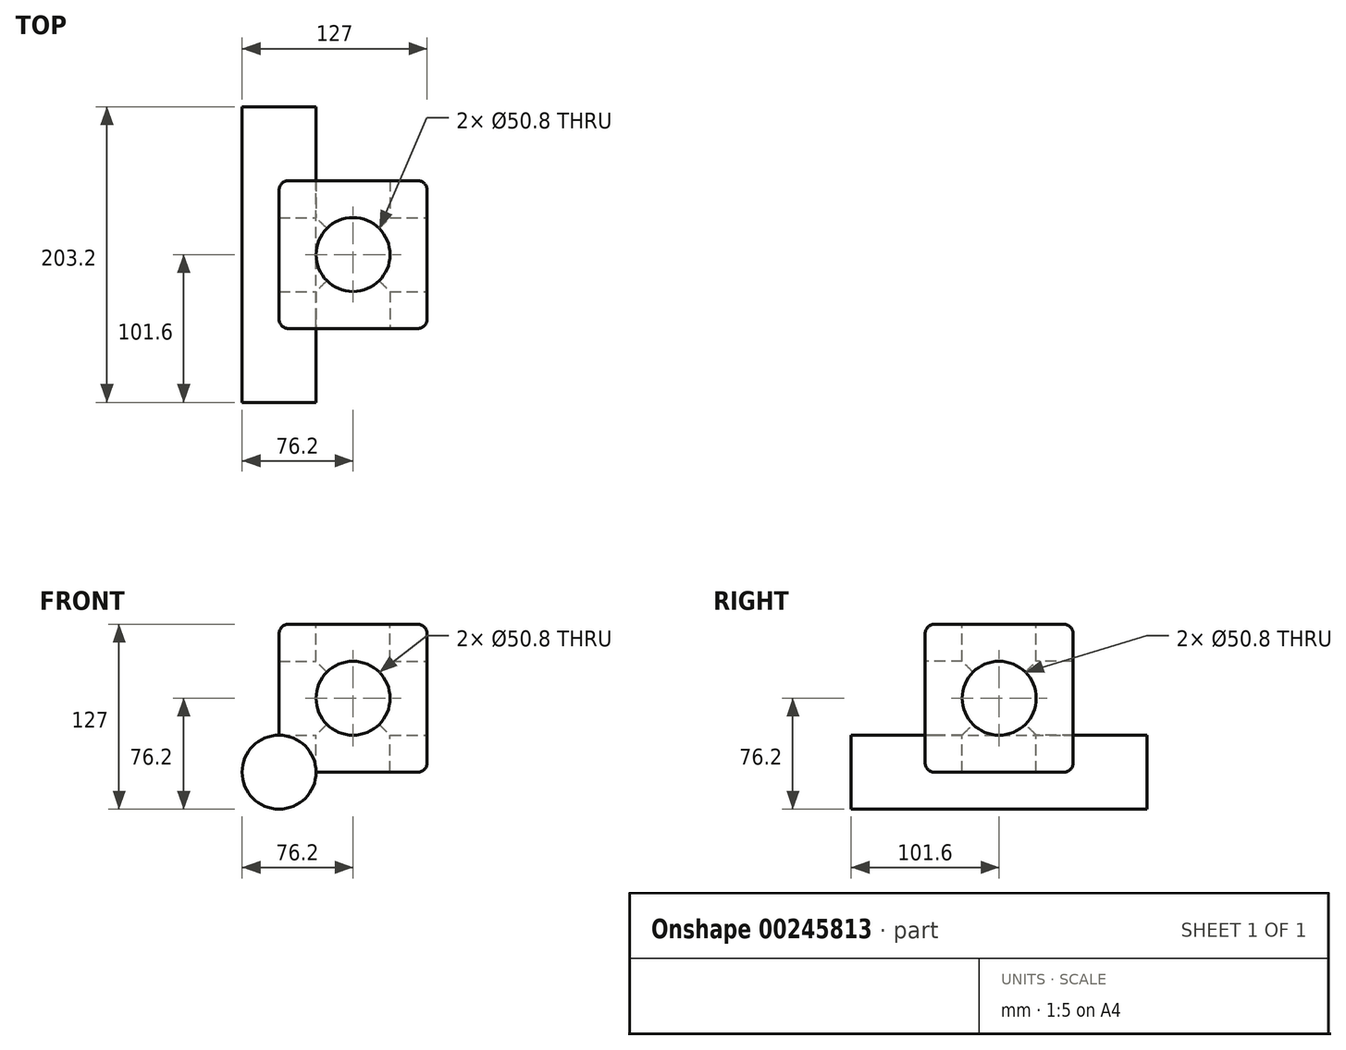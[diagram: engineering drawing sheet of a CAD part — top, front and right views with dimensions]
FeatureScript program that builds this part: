
annotation { "Feature Type Name" : "Feature", "Feature Type Description" : "" }
export const myFeature = defineFeature(function(context is Context, id is Id, definition is map)
    precondition{}
    {
        {
            var Q0;
            Q0=qCreatedBy(makeId("Front.planeOp"),FACE);
            var sketch = newSketch(context, id + "F0", { "sketchPlane" : qUnion([Q0])});
            skLineSegment(sketch, "E0", {"start": v(0, 0) * mm, "end": v(101.6, 0) * mm});
            skLineSegment(sketch, "E1", {"start": v(101.6, 0) * mm, "end": v(101.6, 101.6) * mm});
            skLineSegment(sketch, "E2", {"start": v(101.6, 101.6) * mm, "end": v(0, 101.6) * mm});
            skLineSegment(sketch, "E3", {"start": v(0, 101.6) * mm, "end": v(0, 0) * mm});
            skSolve(sketch);
        }
        {
            var Q0;
            Q0 = qSketchRegion(id + "F0", true);
            extrude(context, id + "F1", {"entities" : qUnion([Q0]), "depth" : 101.6 * mm});
        }
        {
            var Q0;
            Q0=makeQuery(id+"F1.opExtrude","CAP_FACE",FACE,{"disambiguationData":[OSD([sQuery(id+"F0.wireOp",EDGE,"E0"),sQuery(id+"F0.wireOp",EDGE,"E1"),sQuery(id+"F0.wireOp",EDGE,"E2"),sQuery(id+"F0.wireOp",EDGE,"E3")])],"isStart":false});
            var sketch = newSketch(context, id + "F2", { "sketchPlane" : qUnion([Q0])});
            skCircle(sketch, "E4", {"center": v(50.8, 50.8) * mm, "radius": 25.4 * mm});
            skPoint(sketch, "E5.orphan", {"position": v(50.8, 101.6) * mm});
            skPoint(sketch, "E6.end.orphan", {"position": v(50.8, 0) * mm});
            skSolve(sketch);
        }
        {
            var Q0;
            Q0=makeQuery(id+"F2.imprint","IMPRINT",FACE,{"disambiguationData":[TD([[makeQuery(id+"F2.imprint","IMPRINT",EDGE,{"derivedFrom":sQuery(id+"F2.wireOp",EDGE,"E4")}),1.0]])]});
            extrude(context, id + "F3", {"entities" : qUnion([Q0]), "operationType" : NewBodyOperationType.REMOVE, "oppositeDirection" : true, "depth" : 101.6 * mm});
        }
        {
            var Q0;
            Q0=makeQuery(id+"F1.opExtrude","SWEPT_FACE",FACE,{"disambiguationData":[OSD([sQuery(id+"F0.wireOp",EDGE,"E2")])]});
            var sketch = newSketch(context, id + "F4", { "sketchPlane" : qUnion([Q0])});
            skCircle(sketch, "E7", {"center": v(50.8, -50.8) * mm, "radius": 25.4 * mm});
            skPoint(sketch, "E8.orphan", {"position": v(50.8, 0) * mm});
            skPoint(sketch, "E9.end.orphan", {"position": v(50.8, -101.6) * mm});
            skSolve(sketch);
        }
        {
            var Q0;
            Q0=makeQuery(id+"F4.imprint","IMPRINT",FACE,{"disambiguationData":[TD([[makeQuery(id+"F4.imprint","IMPRINT",EDGE,{"derivedFrom":sQuery(id+"F4.wireOp",EDGE,"E7")}),1.0]])]});
            extrude(context, id + "F5", {"entities" : qUnion([Q0]), "operationType" : NewBodyOperationType.REMOVE, "oppositeDirection" : true, "depth" : 101.6 * mm});
        }
        {
            var Q0;
            Q0=makeQuery(id+"F1.opExtrude","SWEPT_FACE",FACE,{"disambiguationData":[OSD([sQuery(id+"F0.wireOp",EDGE,"E1")])]});
            var sketch = newSketch(context, id + "F6", { "sketchPlane" : qUnion([Q0])});
            skCircle(sketch, "E10", {"center": v(-50.8, 50.8) * mm, "radius": 25.4 * mm});
            skPoint(sketch, "E11.orphan", {"position": v(-50.8, 101.6) * mm});
            skPoint(sketch, "E12.end.orphan", {"position": v(-50.8, 0) * mm});
            skSolve(sketch);
        }
        {
            var Q0;
            Q0=makeQuery(id+"F6.imprint","IMPRINT",FACE,{"disambiguationData":[TD([[makeQuery(id+"F6.imprint","IMPRINT",EDGE,{"derivedFrom":sQuery(id+"F6.wireOp",EDGE,"E10")}),1.0]])]});
            extrude(context, id + "F7", {"entities" : qUnion([Q0]), "operationType" : NewBodyOperationType.REMOVE, "oppositeDirection" : true, "depth" : 101.6 * mm});
        }
        {
            var Q0;
            Q0=makeQuery(id+"F1.opExtrude","CAP_EDGE",EDGE,{"disambiguationData":[OSD([sQuery(id+"F0.wireOp",EDGE,"E2")])],"isStart":false});
            var Q1;
            Q1=makeQuery(id+"F1.opExtrude","SWEPT_EDGE",EDGE,{"disambiguationData":[OSD([sQuery(id+"F0.wireOp",EDGE,"E1"),sQuery(id+"F0.wireOp",EDGE,"E2")])]});
            var Q2;
            Q2=makeQuery(id+"F1.opExtrude","CAP_EDGE",EDGE,{"disambiguationData":[OSD([sQuery(id+"F0.wireOp",EDGE,"E1")])],"isStart":false});
            var Q3;
            Q3=makeQuery(id+"F1.opExtrude","SWEPT_EDGE",EDGE,{"disambiguationData":[OSD([sQuery(id+"F0.wireOp",EDGE,"E0"),sQuery(id+"F0.wireOp",EDGE,"E1")])]});
            var Q4;
            Q4=makeQuery(id+"F1.opExtrude","CAP_EDGE",EDGE,{"disambiguationData":[OSD([sQuery(id+"F0.wireOp",EDGE,"E0")])],"isStart":false});
            var Q5;
            Q5=makeQuery(id+"F1.opExtrude","CAP_EDGE",EDGE,{"disambiguationData":[OSD([sQuery(id+"F0.wireOp",EDGE,"E2")])],"isStart":true});
            var Q6;
            Q6=makeQuery(id+"F1.opExtrude","SWEPT_EDGE",EDGE,{"disambiguationData":[OSD([sQuery(id+"F0.wireOp",EDGE,"E2"),sQuery(id+"F0.wireOp",EDGE,"E3")])]});
            var Q7;
            Q7=makeQuery(id+"F1.opExtrude","CAP_EDGE",EDGE,{"disambiguationData":[OSD([sQuery(id+"F0.wireOp",EDGE,"E3")])],"isStart":false});
            var Q8;
            Q8=makeQuery(id+"F1.opExtrude","CAP_EDGE",EDGE,{"disambiguationData":[OSD([sQuery(id+"F0.wireOp",EDGE,"E1")])],"isStart":true});
            var Q9;
            Q9=makeQuery(id+"F1.opExtrude","SWEPT_EDGE",EDGE,{"disambiguationData":[OSD([sQuery(id+"F0.wireOp",EDGE,"E0"),sQuery(id+"F0.wireOp",EDGE,"E3")])]});
            var Q10;
            Q10=makeQuery(id+"F1.opExtrude","CAP_EDGE",EDGE,{"disambiguationData":[OSD([sQuery(id+"F0.wireOp",EDGE,"E3")])],"isStart":true});
            var Q11;
            Q11=makeQuery(id+"F1.opExtrude","CAP_EDGE",EDGE,{"disambiguationData":[OSD([sQuery(id+"F0.wireOp",EDGE,"E0")])],"isStart":true});
            fillet(context, id + "F8", {"entities" : qUnion([Q0, Q1, Q2, Q3, Q4, Q5, Q6, Q7, Q8, Q9, Q10, Q11]), "radius" : 6.35 * mm, "tangentPropagation" : true, "allowEdgeOverflow" : false});
        }
        {
            var Q0;
            Q0=qCreatedBy(makeId("Front.planeOp"),FACE);
            cPlane(context, id + "F9", {"entities" : qUnion([Q0]), "cplaneType" : CPlaneType.OFFSET, "offset" : 101.6 * mm, "width" : 152.4 * mm, "height" : 152.4 * mm});
        }
        {
            var Q0;
            Q0=qCreatedBy(id+"F9.planeOp",FACE);
            var sketch = newSketch(context, id + "F10", { "sketchPlane" : qUnion([Q0])});
            skCircle(sketch, "E13", {"center": v(0, 0) * mm, "radius": 25.4 * mm});
            skSolve(sketch);
        }
        {
            var Q0;
            Q0 = qSketchRegion(id + "F10", true);
            extrude(context, id + "F11", {"entities" : qUnion([Q0]), "operationType" : NewBodyOperationType.ADD, "depth" : 50.8 * mm, "hasSecondDirection" : true, "secondDirectionOppositeDirection" : true, "secondDirectionDepth" : 152.4 * mm});
        }
    });
